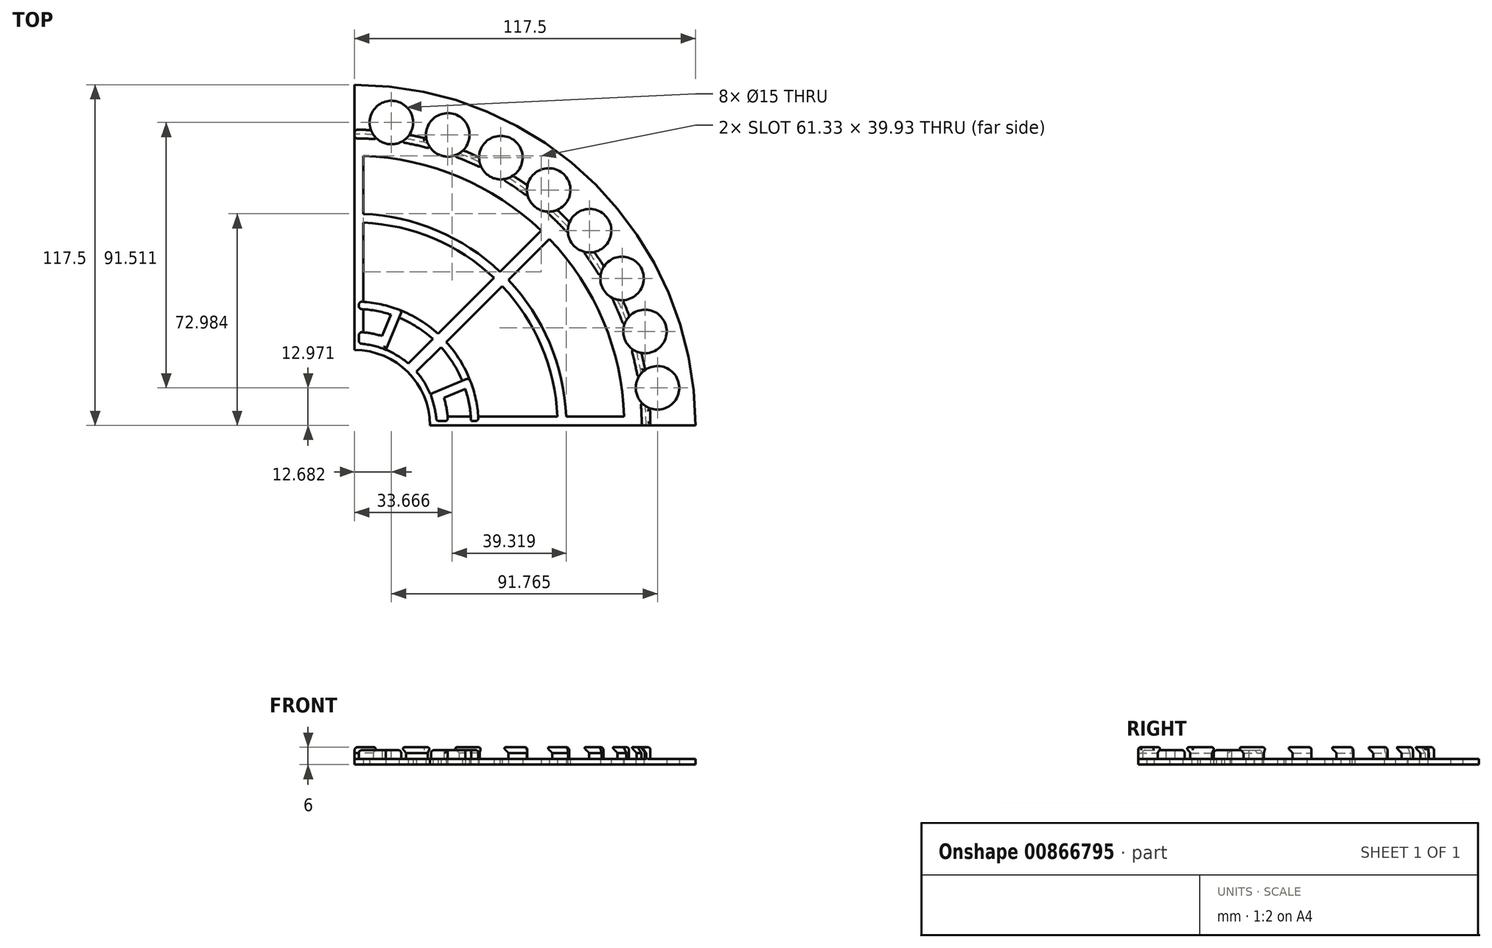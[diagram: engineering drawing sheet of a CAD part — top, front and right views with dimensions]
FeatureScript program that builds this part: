
annotation { "Feature Type Name" : "Feature", "Feature Type Description" : "" }
export const myFeature = defineFeature(function(context is Context, id is Id, definition is map)
    precondition{}
    {
        {
            var Q0;
            Q0=qCreatedBy(makeId("Top.planeOp"),FACE);
            var sketch = newSketch(context, id + "F0", { "sketchPlane" : qUnion([Q0])});
            skCircle(sketch, "E0", {"center": v(0, 0) * mm, "radius": 26 * mm});
            skArc(sketch, "E1", {"start": v(18.5, 21.35) * mm, "mid": v(11.26, 25.9) * mm, "end": v(3, 28.1) * mm});
            skCircle(sketch, "E2", {"center": v(0, 0) * mm, "radius": 42.75 * mm});
            skCircle(sketch, "E3", {"center": v(0, 0) * mm, "radius": 47 * mm});
            skCircle(sketch, "E4", {"center": v(0, 0) * mm, "radius": 93 * mm});
            skCircle(sketch, "E5", {"center": v(0, 0) * mm, "radius": 117.5 * mm});
            skCircle(sketch, "E6", {"center": v(0, 0) * mm, "radius": 36.75 * mm, "construction": true});
            skLineSegment(sketch, "E7", {"start": v(0, 130) * mm, "end": v(0, -133.04) * mm, "construction": true});
            skCircle(sketch, "E8", {"center": v(0, 36.75) * mm, "radius": 3.45 * mm});
            skCircle(sketch, "E9.1.0", {"center": v(-25.99, 25.99) * mm, "radius": 3.45 * mm});
            skCircle(sketch, "E9.2.0", {"center": v(-36.75, 0) * mm, "radius": 3.45 * mm});
            skCircle(sketch, "E9.3.0", {"center": v(-25.99, -25.99) * mm, "radius": 3.45 * mm});
            skCircle(sketch, "E9.4.0", {"center": v(0, -36.75) * mm, "radius": 3.45 * mm});
            skCircle(sketch, "E9.5.0", {"center": v(25.99, -25.99) * mm, "radius": 3.45 * mm});
            skCircle(sketch, "E9.6.0", {"center": v(36.75, 0) * mm, "radius": 3.45 * mm});
            skCircle(sketch, "E9.7.0", {"center": v(25.99, 25.99) * mm, "radius": 3.45 * mm});
            skLineSegment(sketch, "E10", {"start": v(3, 92.95) * mm, "end": v(3, 28.1) * mm});
            skLineSegment(sketch, "E11", {"start": v(28.1, 3) * mm, "end": v(92.95, 3) * mm});
            skCircle(sketch, "E12", {"center": v(0, 0) * mm, "radius": 70 * mm});
            skCircle(sketch, "E13", {"center": v(0, 0) * mm, "radius": 73 * mm});
            skLineSegment(sketch, "E14", {"start": v(0, 0) * mm, "end": v(83.09, 83.09) * mm, "construction": true});
            skLineSegment(sketch, "E15.trimOffspring", {"start": v(18.5, 21.35) * mm, "end": v(64.33, 67.16) * mm});
            skLineSegment(sketch, "E16.trimOffspring", {"start": v(21.35, 18.5) * mm, "end": v(67.16, 64.33) * mm});
            skCircle(sketch, "E17", {"center": v(0, 0) * mm, "radius": 40.2 * mm});
            skLineSegment(sketch, "E18", {"start": v(0, 0) * mm, "end": v(52.17, 125.95) * mm, "construction": true});
            skLineSegment(sketch, "E19.MirrorCS", {"start": v(0, 0) * mm, "end": v(125.95, 52.17) * mm, "construction": true});
            skLineSegment(sketch, "E20", {"start": v(0, 26) * mm, "end": v(0, 117.5) * mm});
            skLineSegment(sketch, "E21", {"start": v(26, 0) * mm, "end": v(93, 0) * mm});
            skCircle(sketch, "E22", {"center": v(0, 0) * mm, "radius": 32.25 * mm});
            skPoint(sketch, "E23", {"position": v(117.5, 0) * mm});
            skPoint(sketch, "E24", {"position": v(0, 93) * mm});
            skLineSegment(sketch, "E25", {"start": v(93, 0) * mm, "end": v(110.05, 0) * mm});
            skLineSegment(sketch, "E26", {"start": v(110.05, 0) * mm, "end": v(117.5, 0) * mm});
            skLineSegment(sketch, "E27.trimOffspring", {"start": v(81.66, 84.48) * mm, "end": v(81.85, 84.67) * mm});
            skLineSegment(sketch, "E28.trimOffspring", {"start": v(84.48, 81.66) * mm, "end": v(84.67, 81.85) * mm});
            skArc(sketch, "E29.trimOffspring", {"start": v(28.1, 3) * mm, "mid": v(25.9, 11.26) * mm, "end": v(21.35, 18.5) * mm});
            skArc(sketch, "E30.trimOffspring", {"start": v(0, 28.25) * mm, "mid": v(-19.98, -19.98) * mm, "end": v(28.25, 0) * mm});
            skSolve(sketch);
        }
        {
            var Q0;
            {var subQ10=sQuery(id+"F0.wireOp",EDGE,"E25");Q0=makeQuery(id+"F0.imprint","IMPRINT",FACE,{"disambiguationData":[TD([[makeQuery(id+"F0.imprint","IMPRINT",EDGE,{"derivedFrom":subQ10}),1.0]])]});}
            var Q1;
            {var subQ0=sQuery(id+"F0.wireOp",EDGE,"E10");var subQ1=sQuery(id+"F0.wireOp",EDGE,"E4");var subQ2=makeQuery(id+"F0.imprint","INTERSECT",VERTEX,{"derivedFrom":[subQ1,subQ0]});Q1=makeQuery(id+"F0.imprint","IMPRINT",FACE,{"disambiguationData":[TD([[makeQuery(id+"F0.imprint","IMPRINT",EDGE,{"disambiguationData":[TD([[subQ2,-1.0]])],"derivedFrom":subQ1}),1.0]])]});}
            var Q2;
            {var subQ0=sQuery(id+"F0.wireOp",EDGE,"E13");var subQ1=sQuery(id+"F0.wireOp",EDGE,"E10");var subQ2=makeQuery(id+"F0.imprint","INTERSECT",VERTEX,{"derivedFrom":[subQ1,subQ0]});Q2=makeQuery(id+"F0.imprint","IMPRINT",FACE,{"disambiguationData":[TD([[makeQuery(id+"F0.imprint","IMPRINT",EDGE,{"disambiguationData":[TD([[subQ2,-1.0]])],"derivedFrom":subQ1}),-1.0]])]});}
            var Q3;
            {var subQ0=sQuery(id+"F0.wireOp",EDGE,"E10");var subQ1=sQuery(id+"F0.wireOp",EDGE,"E3");var subQ2=makeQuery(id+"F0.imprint","INTERSECT",VERTEX,{"derivedFrom":[subQ1,subQ0]});Q3=makeQuery(id+"F0.imprint","IMPRINT",FACE,{"disambiguationData":[TD([[makeQuery(id+"F0.imprint","IMPRINT",EDGE,{"disambiguationData":[TD([[subQ2,-1.0]])],"derivedFrom":subQ1}),-1.0]])]});}
            var Q4;
            {var subQ0=sQuery(id+"F0.wireOp",EDGE,"E10");var subQ1=sQuery(id+"F0.wireOp",EDGE,"E2");var subQ2=makeQuery(id+"F0.imprint","INTERSECT",VERTEX,{"derivedFrom":[subQ1,subQ0]});Q4=makeQuery(id+"F0.imprint","IMPRINT",FACE,{"disambiguationData":[TD([[makeQuery(id+"F0.imprint","IMPRINT",EDGE,{"disambiguationData":[TD([[subQ2,-1.0]])],"derivedFrom":subQ1}),-1.0]])]});}
            var Q5;
            {var subQ0=sQuery(id+"F0.wireOp",EDGE,"E10");var subQ1=sQuery(id+"F0.wireOp",EDGE,"E2");var subQ2=makeQuery(id+"F0.imprint","INTERSECT",VERTEX,{"derivedFrom":[subQ1,subQ0]});Q5=makeQuery(id+"F0.imprint","IMPRINT",FACE,{"disambiguationData":[TD([[makeQuery(id+"F0.imprint","IMPRINT",EDGE,{"disambiguationData":[TD([[subQ2,-1.0]])],"derivedFrom":subQ1}),1.0]])]});}
            var Q6;
            {var subQ1=sQuery(id+"F0.wireOp",EDGE,"E8");var subQ3=sQuery(id+"F0.wireOp",EDGE,"E20");var subQ5=makeQuery(id+"F0.imprint","INTERSECT",VERTEX,{"derivedFrom":[subQ1,subQ3]});Q6=makeQuery(id+"F0.imprint","IMPRINT",FACE,{"disambiguationData":[TD([[makeQuery(id+"F0.imprint","IMPRINT",EDGE,{"disambiguationData":[TD([[subQ5,-1.0]])],"derivedFrom":subQ1}),1.0]])]});}
            var Q7;
            {var subQ0=sQuery(id+"F0.wireOp",EDGE,"E10");var subQ1=sQuery(id+"F0.wireOp",EDGE,"E8");var subQ2=makeQuery(id+"F0.imprint","INTERSECT",VERTEX,{"disambiguationData":[OD(0.0)],"derivedFrom":[subQ1,subQ0]});Q7=makeQuery(id+"F0.imprint","IMPRINT",FACE,{"disambiguationData":[TD([[makeQuery(id+"F0.imprint","IMPRINT",EDGE,{"disambiguationData":[TD([[subQ2,1.0]])],"derivedFrom":subQ0}),-1.0]])]});}
            var Q8;
            {var subQ0=sQuery(id+"F0.wireOp",EDGE,"E20");var subQ1=sQuery(id+"F0.wireOp",EDGE,"E8");var subQ2=makeQuery(id+"F0.imprint","INTERSECT",VERTEX,{"derivedFrom":[subQ1,subQ0]});Q8=makeQuery(id+"F0.imprint","IMPRINT",FACE,{"disambiguationData":[TD([[makeQuery(id+"F0.imprint","IMPRINT",EDGE,{"disambiguationData":[TD([[subQ2,-1.0]])],"derivedFrom":subQ1}),-1.0]])]});}
            var Q9;
            {var subQ16=sQuery(id+"F0.wireOp",EDGE,"E1");Q9=makeQuery(id+"F0.imprint","IMPRINT",FACE,{"disambiguationData":[TD([[makeQuery(id+"F0.imprint","IMPRINT",EDGE,{"derivedFrom":subQ16}),1.0]])]});}
            var Q10;
            {var subQ0=sQuery(id+"F0.wireOp",EDGE,"E15.trimOffspring");var subQ1=sQuery(id+"F0.wireOp",EDGE,"E9.7.0");var subQ2=makeQuery(id+"F0.imprint","INTERSECT",VERTEX,{"disambiguationData":[OD(1.0)],"derivedFrom":[subQ1,subQ0]});Q10=makeQuery(id+"F0.imprint","IMPRINT",FACE,{"disambiguationData":[TD([[makeQuery(id+"F0.imprint","IMPRINT",EDGE,{"disambiguationData":[TD([[subQ2,-1.0]])],"derivedFrom":subQ1}),-1.0]])]});}
            var Q11;
            {var subQ1=sQuery(id+"F0.wireOp",EDGE,"E9.7.0");var subQ6=makeQuery(id+"F0.imprint","INTERSECT",VERTEX,{"derivedFrom":[subQ1,sQuery(id+"F0.wireOp",EDGE,"E17")]});Q11=makeQuery(id+"F0.imprint","IMPRINT",FACE,{"disambiguationData":[TD([[makeQuery(id+"F0.imprint","IMPRINT",EDGE,{"disambiguationData":[TD([[subQ6,1.0]])],"derivedFrom":subQ1}),1.0]])]});}
            var Q12;
            {var subQ2=sQuery(id+"F0.wireOp",EDGE,"E16.trimOffspring");var subQ4=sQuery(id+"F0.wireOp",EDGE,"E2");var subQ5=makeQuery(id+"F0.imprint","INTERSECT",VERTEX,{"derivedFrom":[subQ4,subQ2]});Q12=makeQuery(id+"F0.imprint","IMPRINT",FACE,{"disambiguationData":[TD([[makeQuery(id+"F0.imprint","IMPRINT",EDGE,{"disambiguationData":[TD([[subQ5,-1.0]])],"derivedFrom":subQ4}),1.0]])]});}
            var Q13;
            {var subQ0=sQuery(id+"F0.wireOp",EDGE,"E17");var subQ1=sQuery(id+"F0.wireOp",EDGE,"E9.7.0");var subQ2=makeQuery(id+"F0.imprint","INTERSECT",VERTEX,{"derivedFrom":[subQ1,subQ0]});Q13=makeQuery(id+"F0.imprint","IMPRINT",FACE,{"disambiguationData":[TD([[makeQuery(id+"F0.imprint","IMPRINT",EDGE,{"disambiguationData":[TD([[subQ2,-1.0]])],"derivedFrom":subQ1}),-1.0]])]});}
            var Q14;
            {var subQ0=sQuery(id+"F0.wireOp",EDGE,"E17");var subQ1=sQuery(id+"F0.wireOp",EDGE,"E9.7.0");var subQ2=makeQuery(id+"F0.imprint","INTERSECT",VERTEX,{"derivedFrom":[subQ1,subQ0]});Q14=makeQuery(id+"F0.imprint","IMPRINT",FACE,{"disambiguationData":[TD([[makeQuery(id+"F0.imprint","IMPRINT",EDGE,{"disambiguationData":[TD([[subQ2,1.0]])],"derivedFrom":subQ1}),-1.0]])]});}
            var Q15;
            {var subQ0=sQuery(id+"F0.wireOp",EDGE,"E16.trimOffspring");var subQ1=sQuery(id+"F0.wireOp",EDGE,"E2");var subQ2=makeQuery(id+"F0.imprint","INTERSECT",VERTEX,{"derivedFrom":[subQ1,subQ0]});Q15=makeQuery(id+"F0.imprint","IMPRINT",FACE,{"disambiguationData":[TD([[makeQuery(id+"F0.imprint","IMPRINT",EDGE,{"disambiguationData":[TD([[subQ2,-1.0]])],"derivedFrom":subQ1}),-1.0]])]});}
            var Q16;
            {var subQ0=sQuery(id+"F0.wireOp",EDGE,"E16.trimOffspring");var subQ1=sQuery(id+"F0.wireOp",EDGE,"E3");var subQ2=makeQuery(id+"F0.imprint","INTERSECT",VERTEX,{"derivedFrom":[subQ1,subQ0]});Q16=makeQuery(id+"F0.imprint","IMPRINT",FACE,{"disambiguationData":[TD([[makeQuery(id+"F0.imprint","IMPRINT",EDGE,{"disambiguationData":[TD([[subQ2,-1.0]])],"derivedFrom":subQ1}),-1.0]])]});}
            var Q17;
            {var subQ0=sQuery(id+"F0.wireOp",EDGE,"E16.trimOffspring");var subQ1=sQuery(id+"F0.wireOp",EDGE,"E12");var subQ2=makeQuery(id+"F0.imprint","INTERSECT",VERTEX,{"derivedFrom":[subQ1,subQ0]});Q17=makeQuery(id+"F0.imprint","IMPRINT",FACE,{"disambiguationData":[TD([[makeQuery(id+"F0.imprint","IMPRINT",EDGE,{"disambiguationData":[TD([[subQ2,-1.0]])],"derivedFrom":subQ1}),-1.0]])]});}
            var Q18;
            {var subQ0=sQuery(id+"F0.wireOp",EDGE,"E13");var subQ1=sQuery(id+"F0.wireOp",EDGE,"E10");var subQ2=makeQuery(id+"F0.imprint","INTERSECT",VERTEX,{"derivedFrom":[subQ1,subQ0]});Q18=makeQuery(id+"F0.imprint","IMPRINT",FACE,{"disambiguationData":[TD([[makeQuery(id+"F0.imprint","IMPRINT",EDGE,{"disambiguationData":[TD([[subQ2,-1.0]])],"derivedFrom":subQ1}),1.0]])]});}
            var Q19;
            {var subQ0=sQuery(id+"F0.wireOp",EDGE,"E15.trimOffspring");var subQ1=sQuery(id+"F0.wireOp",EDGE,"E4");var subQ2=makeQuery(id+"F0.imprint","INTERSECT",VERTEX,{"derivedFrom":[subQ1,subQ0]});Q19=makeQuery(id+"F0.imprint","IMPRINT",FACE,{"disambiguationData":[TD([[makeQuery(id+"F0.imprint","IMPRINT",EDGE,{"disambiguationData":[TD([[subQ2,1.0]])],"derivedFrom":subQ1}),1.0]])]});}
            var Q20;
            {var subQ0=sQuery(id+"F0.wireOp",EDGE,"E12");var subQ1=sQuery(id+"F0.wireOp",EDGE,"E11");var subQ2=makeQuery(id+"F0.imprint","INTERSECT",VERTEX,{"derivedFrom":[subQ1,subQ0]});Q20=makeQuery(id+"F0.imprint","IMPRINT",FACE,{"disambiguationData":[TD([[makeQuery(id+"F0.imprint","IMPRINT",EDGE,{"disambiguationData":[TD([[subQ2,-1.0]])],"derivedFrom":subQ1}),1.0]])]});}
            var Q21;
            {var subQ0=sQuery(id+"F0.wireOp",EDGE,"E11");var subQ1=sQuery(id+"F0.wireOp",EDGE,"E9.6.0");var subQ2=makeQuery(id+"F0.imprint","INTERSECT",VERTEX,{"disambiguationData":[OD(1.0)],"derivedFrom":[subQ1,subQ0]});Q21=makeQuery(id+"F0.imprint","IMPRINT",FACE,{"disambiguationData":[TD([[makeQuery(id+"F0.imprint","IMPRINT",EDGE,{"disambiguationData":[TD([[subQ2,-1.0]])],"derivedFrom":subQ1}),-1.0]])]});}
            var Q22;
            {var subQ0=sQuery(id+"F0.wireOp",EDGE,"E11");var subQ1=sQuery(id+"F0.wireOp",EDGE,"E9.6.0");var subQ5=makeQuery(id+"F0.imprint","INTERSECT",VERTEX,{"disambiguationData":[OD(1.0)],"derivedFrom":[subQ1,subQ0]});Q22=makeQuery(id+"F0.imprint","IMPRINT",FACE,{"disambiguationData":[TD([[makeQuery(id+"F0.imprint","IMPRINT",EDGE,{"disambiguationData":[TD([[subQ5,-1.0]])],"derivedFrom":subQ1}),1.0]])]});}
            var Q23;
            {var subQ0=sQuery(id+"F0.wireOp",EDGE,"E11");var subQ1=sQuery(id+"F0.wireOp",EDGE,"E9.6.0");var subQ2=makeQuery(id+"F0.imprint","INTERSECT",VERTEX,{"disambiguationData":[OD(0.0)],"derivedFrom":[subQ1,subQ0]});Q23=makeQuery(id+"F0.imprint","IMPRINT",FACE,{"disambiguationData":[TD([[makeQuery(id+"F0.imprint","IMPRINT",EDGE,{"disambiguationData":[TD([[subQ2,-1.0]])],"derivedFrom":subQ0}),-1.0]])]});}
            var Q24;
            {var subQ0=sQuery(id+"F0.wireOp",EDGE,"E11");var subQ1=sQuery(id+"F0.wireOp",EDGE,"E2");var subQ2=makeQuery(id+"F0.imprint","INTERSECT",VERTEX,{"derivedFrom":[subQ1,subQ0]});Q24=makeQuery(id+"F0.imprint","IMPRINT",FACE,{"disambiguationData":[TD([[makeQuery(id+"F0.imprint","IMPRINT",EDGE,{"disambiguationData":[TD([[subQ2,1.0]])],"derivedFrom":subQ1}),1.0]])]});}
            var Q25;
            {var subQ0=sQuery(id+"F0.wireOp",EDGE,"E11");var subQ1=sQuery(id+"F0.wireOp",EDGE,"E2");var subQ2=makeQuery(id+"F0.imprint","INTERSECT",VERTEX,{"derivedFrom":[subQ1,subQ0]});Q25=makeQuery(id+"F0.imprint","IMPRINT",FACE,{"disambiguationData":[TD([[makeQuery(id+"F0.imprint","IMPRINT",EDGE,{"disambiguationData":[TD([[subQ2,1.0]])],"derivedFrom":subQ1}),-1.0]])]});}
            var Q26;
            {var subQ0=sQuery(id+"F0.wireOp",EDGE,"E11");var subQ1=sQuery(id+"F0.wireOp",EDGE,"E3");var subQ2=makeQuery(id+"F0.imprint","INTERSECT",VERTEX,{"derivedFrom":[subQ1,subQ0]});Q26=makeQuery(id+"F0.imprint","IMPRINT",FACE,{"disambiguationData":[TD([[makeQuery(id+"F0.imprint","IMPRINT",EDGE,{"disambiguationData":[TD([[subQ2,1.0]])],"derivedFrom":subQ1}),-1.0]])]});}
            var Q27;
            {var subQ0=sQuery(id+"F0.wireOp",EDGE,"E12");var subQ1=sQuery(id+"F0.wireOp",EDGE,"E11");var subQ2=makeQuery(id+"F0.imprint","INTERSECT",VERTEX,{"derivedFrom":[subQ1,subQ0]});Q27=makeQuery(id+"F0.imprint","IMPRINT",FACE,{"disambiguationData":[TD([[makeQuery(id+"F0.imprint","IMPRINT",EDGE,{"disambiguationData":[TD([[subQ2,-1.0]])],"derivedFrom":subQ1}),-1.0]])]});}
            var Q28;
            {var subQ0=sQuery(id+"F0.wireOp",EDGE,"E11");var subQ1=sQuery(id+"F0.wireOp",EDGE,"E4");var subQ2=makeQuery(id+"F0.imprint","INTERSECT",VERTEX,{"derivedFrom":[subQ1,subQ0]});Q28=makeQuery(id+"F0.imprint","IMPRINT",FACE,{"disambiguationData":[TD([[makeQuery(id+"F0.imprint","IMPRINT",EDGE,{"disambiguationData":[TD([[subQ2,1.0]])],"derivedFrom":subQ0}),-1.0]])]});}
            var Q29;
            {var subQ0=sQuery(id+"F0.wireOp",EDGE,"E15.trimOffspring");var subQ1=sQuery(id+"F0.wireOp",EDGE,"E2");var subQ2=makeQuery(id+"F0.imprint","INTERSECT",VERTEX,{"derivedFrom":[subQ1,subQ0]});Q29=makeQuery(id+"F0.imprint","IMPRINT",FACE,{"disambiguationData":[TD([[makeQuery(id+"F0.imprint","IMPRINT",EDGE,{"disambiguationData":[TD([[subQ2,-1.0]])],"derivedFrom":subQ1}),1.0]])]});}
            var Q30;
            {var subQ0=sQuery(id+"F0.wireOp",EDGE,"E11");var subQ1=sQuery(id+"F0.wireOp",EDGE,"E2");var subQ2=makeQuery(id+"F0.imprint","INTERSECT",VERTEX,{"derivedFrom":[subQ1,subQ0]});Q30=makeQuery(id+"F0.imprint","IMPRINT",FACE,{"disambiguationData":[TD([[makeQuery(id+"F0.imprint","IMPRINT",EDGE,{"disambiguationData":[TD([[subQ2,-1.0]])],"derivedFrom":subQ1}),1.0]])]});}
            extrude(context, id + "F1", {"entities" : qUnion([Q0, Q1, Q2, Q3, Q4, Q5, Q6, Q7, Q8, Q9, Q10, Q11, Q12, Q13, Q14, Q15, Q16, Q17, Q18, Q19, Q20, Q21, Q22, Q23, Q24, Q25, Q26, Q27, Q28, Q29, Q30]), "depth" : 2 * mm, "offsetDistance" : 25 * mm});
        }
        {
            var Q0;
            Q0=qCreatedBy(makeId("Top.planeOp"),FACE);
            var sketch = newSketch(context, id + "F2", { "sketchPlane" : qUnion([Q0])});
            skLineSegment(sketch, "E31.2", {"start": v(26.1, 10.81) * mm, "end": v(39.5, 16.36) * mm});
            skLineSegment(sketch, "E31.3", {"start": v(10.81, 26.1) * mm, "end": v(16.36, 39.5) * mm});
            skArc(sketch, "E32.1", {"start": v(10.81, 26.1) * mm, "mid": v(6.25, 27.55) * mm, "end": v(1.5, 28.21) * mm});
            skArc(sketch, "E32.2", {"start": v(28.21, 1.5) * mm, "mid": v(27.55, 6.25) * mm, "end": v(26.1, 10.81) * mm});
            skArc(sketch, "E32.3", {"start": v(16.36, 39.5) * mm, "mid": v(9.07, 41.78) * mm, "end": v(1.5, 42.72) * mm});
            skArc(sketch, "E32.4", {"start": v(12.57, 38.18) * mm, "mid": v(7.1, 39.57) * mm, "end": v(1.5, 40.17) * mm});
            skLineSegment(sketch, "E33.0", {"start": v(1.5, 28.21) * mm, "end": v(1.5, 32.22) * mm});
            skLineSegment(sketch, "E34.0", {"start": v(28.21, 1.5) * mm, "end": v(32.22, 1.5) * mm});
            skArc(sketch, "E35.trimOffspring", {"start": v(42.72, 1.5) * mm, "mid": v(41.78, 9.07) * mm, "end": v(39.5, 16.36) * mm});
            skArc(sketch, "E36.trimOffspring", {"start": v(40.17, 1.5) * mm, "mid": v(39.57, 7.1) * mm, "end": v(38.18, 12.57) * mm});
            skLineSegment(sketch, "E37.0", {"start": v(9.52, 30.81) * mm, "end": v(12.57, 38.18) * mm});
            skLineSegment(sketch, "E38.0", {"start": v(30.81, 9.52) * mm, "end": v(38.18, 12.57) * mm});
            skPoint(sketch, "E39.orphan", {"position": v(3, 40.09) * mm});
            skPoint(sketch, "E40.orphan", {"position": v(3, 28.1) * mm});
            skPoint(sketch, "E41.orphan", {"position": v(28.1, 3) * mm});
            skPoint(sketch, "E42.orphan", {"position": v(40.09, 3) * mm});
            skPoint(sketch, "E43.orphan", {"position": v(0, 26) * mm});
            skPoint(sketch, "E44.orphan", {"position": v(26, 0) * mm});
            skCircle(sketch, "E45.0", {"center": v(36.75, 0) * mm, "radius": 3.45 * mm, "construction": true});
            skArc(sketch, "E46.0", {"start": v(32.22, 1.5) * mm, "mid": v(31.77, 5.55) * mm, "end": v(30.81, 9.52) * mm});
            skCircle(sketch, "E47.1", {"center": v(0, 36.75) * mm, "radius": 3.45 * mm, "construction": true});
            skLineSegment(sketch, "E48.trimOffspring", {"start": v(40.17, 1.5) * mm, "end": v(42.72, 1.5) * mm});
            skLineSegment(sketch, "E49.trimOffspring", {"start": v(1.5, 40.17) * mm, "end": v(1.5, 42.72) * mm});
            skArc(sketch, "E50.trimOffspring", {"start": v(9.52, 30.81) * mm, "mid": v(5.55, 31.77) * mm, "end": v(1.5, 32.22) * mm});
            skSolve(sketch);
        }
        {
            var Q0;
            Q0 = qSketchRegion(id + "F2", true);
            extrude(context, id + "F3", {"entities" : qUnion([Q0]), "operationType" : NewBodyOperationType.ADD, "depth" : 5 * mm, "offsetDistance" : 25 * mm});
        }
        {
            var Q0;
            Q0=makeQuery(id+"F1.opExtrude","SWEPT_FACE",FACE,{"disambiguationData":[OSD([sQuery(id+"F0.wireOp",EDGE,"E20")])]});
            var sketch = newSketch(context, id + "F4", { "sketchPlane" : qUnion([Q0])});
            skLineSegment(sketch, "E51", {"start": v(-102, 6) * mm, "end": v(-99, 6) * mm});
            skLineSegment(sketch, "E52.0", {"start": v(-42.75, 2) * mm, "end": v(-117.5, 2) * mm});
            skLineSegment(sketch, "E53", {"start": v(-102, 6) * mm, "end": v(-102, 2) * mm});
            skLineSegment(sketch, "E54", {"start": v(-100.5, 2) * mm, "end": v(-100.5, 4) * mm});
            skLineSegment(sketch, "E55", {"start": v(-100.5, 4) * mm, "end": v(-99, 6) * mm});
            skSolve(sketch);
        }
        {
            var Q0;
            Q0=qCreatedBy(makeId("Front.planeOp"),FACE);
            var sketch = newSketch(context, id + "F5", { "sketchPlane" : qUnion([Q0])});
            skLineSegment(sketch, "E56", {"start": v(0, 34.31) * mm, "end": v(0, -23.12) * mm, "construction": true});
            skSolve(sketch);
        }
        {
            var Q0;
            Q0=makeQuery(id+"F4.imprint","IMPRINT",FACE,{"disambiguationData":[TD([[makeQuery(id+"F4.imprint","IMPRINT",EDGE,{"derivedFrom":sQuery(id+"F4.wireOp",EDGE,"E51")}),-1.0]])]});
            var Q1;
            Q1=sQuery(id+"F5.wireOp",EDGE,"E56");
            revolve(context, id + "F6", {"operationType" : NewBodyOperationType.ADD, "surfaceOperationType" : NewSurfaceOperationType.NEW, "entities" : qUnion([Q0]), "axis" : qUnion([Q1]), "revolveType" : RevolveType.FULL});
        }
        {
            var Q0;
            {var subQ0=sQuery(id+"F0.wireOp",EDGE,"E20");var subQ3=sQuery(id+"F0.wireOp",EDGE,"E26");var subQ4=sQuery(id+"F0.wireOp",EDGE,"E25");var subQ5=sQuery(id+"F0.wireOp",EDGE,"E21");var subQ7=sQuery(id+"F0.wireOp",EDGE,"E5");var subQ8=makeQuery(id+"F1.opExtrude","SWEPT_FACE",FACE,{"disambiguationData":[OSD([subQ7])]});var subQ10=sQuery(id+"F0.wireOp",EDGE,"E17");var subQ11=sQuery(id+"F0.wireOp",EDGE,"E11");var subQ12=sQuery(id+"F0.wireOp",EDGE,"E16.trimOffspring");var subQ14=sQuery(id+"F0.wireOp",EDGE,"E4");var subQ16=sQuery(id+"F0.wireOp",EDGE,"E13");var subQ23=sQuery(id+"F0.wireOp",EDGE,"E29.trimOffspring");var subQ24=sQuery(id+"F0.wireOp",EDGE,"E15.trimOffspring");var subQ29=sQuery(id+"F0.wireOp",EDGE,"E12");var subQ31=sQuery(id+"F0.wireOp",EDGE,"E2");var subQ37=sQuery(id+"F0.wireOp",EDGE,"E1");var subQ38=sQuery(id+"F0.wireOp",EDGE,"E10");var subQ49=sQuery(id+"F0.wireOp",EDGE,"E0");Q0=makeQuery(id+"F6.boolean.opBoolean","SPLIT",FACE,{"disambiguationData":[TD([subQ8])],"derivedFrom":makeQuery(id+"F3.boolean.opBoolean","SPLIT",FACE,{"disambiguationData":[TD([makeQuery(id+"F1.opExtrude","SWEPT_FACE",FACE,{"disambiguationData":[OSD([subQ49])]})])],"derivedFrom":makeQuery(id+"F1.opExtrude","CAP_FACE",FACE,{"disambiguationData":[OSD([subQ49,subQ37,subQ31,subQ14,subQ7,subQ38,subQ11,subQ29,subQ16,subQ24,subQ12,subQ10,subQ0,subQ5,subQ4,subQ3,subQ23])],"isStart":false})})});}
            var sketch = newSketch(context, id + "F7", { "sketchPlane" : qUnion([Q0])});
            skCircle(sketch, "E57.0", {"center": v(0, 0) * mm, "radius": 102 * mm});
            skCircle(sketch, "E57.1", {"center": v(0, 0) * mm, "radius": 99 * mm});
            skLineSegment(sketch, "E57.2", {"start": v(93, 0) * mm, "end": v(110.05, 0) * mm});
            skLineSegment(sketch, "E57.3", {"start": v(0, 42.75) * mm, "end": v(0, 117.5) * mm});
            skSolve(sketch);
        }
        {
            var Q0;
            {var subQ0=sQuery(id+"F7.wireOp",EDGE,"E57.3");var subQ1=sQuery(id+"F7.wireOp",EDGE,"E57.0");var subQ2=makeQuery(id+"F7.imprint","INTERSECT",VERTEX,{"derivedFrom":[subQ1,subQ0]});Q0=makeQuery(id+"F7.imprint","IMPRINT",FACE,{"disambiguationData":[TD([[makeQuery(id+"F7.imprint","IMPRINT",EDGE,{"disambiguationData":[TD([[subQ2,-1.0]])],"derivedFrom":subQ1}),1.0]])]});}
            extrude(context, id + "F8", {"entities" : qUnion([Q0]), "operationType" : NewBodyOperationType.REMOVE, "endBound" : BoundingType.THROUGH_ALL, "depth" : 25 * mm, "offsetDistance" : 25 * mm});
        }
        {
            var Q0;
            Q0=makeQuery(id+"F3.boolean.opBoolean","MERGE",FACE,{"derivedFrom":[makeQuery(id+"F1.opExtrude","CAP_FACE",FACE,{"disambiguationData":[OSD([sQuery(id+"F0.wireOp",EDGE,"E0"),sQuery(id+"F0.wireOp",EDGE,"E1"),sQuery(id+"F0.wireOp",EDGE,"E2"),sQuery(id+"F0.wireOp",EDGE,"E4"),sQuery(id+"F0.wireOp",EDGE,"E5"),sQuery(id+"F0.wireOp",EDGE,"E10"),sQuery(id+"F0.wireOp",EDGE,"E11"),sQuery(id+"F0.wireOp",EDGE,"E12"),sQuery(id+"F0.wireOp",EDGE,"E13"),sQuery(id+"F0.wireOp",EDGE,"E15.trimOffspring"),sQuery(id+"F0.wireOp",EDGE,"E16.trimOffspring"),sQuery(id+"F0.wireOp",EDGE,"E17"),sQuery(id+"F0.wireOp",EDGE,"E20"),sQuery(id+"F0.wireOp",EDGE,"E21"),sQuery(id+"F0.wireOp",EDGE,"E25"),sQuery(id+"F0.wireOp",EDGE,"E26"),sQuery(id+"F0.wireOp",EDGE,"E29.trimOffspring")])],"isStart":true}),makeQuery(id+"F3.opExtrude","CAP_FACE",FACE,{"disambiguationData":[OSD([sQuery(id+"F2.wireOp",EDGE,"E31.0"),sQuery(id+"F2.wireOp",EDGE,"E31.3"),sQuery(id+"F2.wireOp",EDGE,"E32.1"),sQuery(id+"F2.wireOp",EDGE,"E32.3"),sQuery(id+"F2.wireOp",EDGE,"E32.4"),sQuery(id+"F2.wireOp",EDGE,"E33.0"),sQuery(id+"F2.wireOp",EDGE,"8e3e6910-3747-4ed9-b88e-42e2a95604ab.trimOffspring"),sQuery(id+"F2.wireOp",EDGE,"E37.0")])],"isStart":true}),makeQuery(id+"F3.opExtrude","CAP_FACE",FACE,{"disambiguationData":[OSD([sQuery(id+"F2.wireOp",EDGE,"E31.1"),sQuery(id+"F2.wireOp",EDGE,"E31.2"),sQuery(id+"F2.wireOp",EDGE,"E32.0"),sQuery(id+"F2.wireOp",EDGE,"E32.2"),sQuery(id+"F2.wireOp",EDGE,"E34.0"),sQuery(id+"F2.wireOp",EDGE,"E35.trimOffspring"),sQuery(id+"F2.wireOp",EDGE,"E36.trimOffspring"),sQuery(id+"F2.wireOp",EDGE,"E38.0")])],"isStart":true})]});
            var sketch = newSketch(context, id + "F9", { "sketchPlane" : qUnion([Q0])});
            skArc(sketch, "E58.0", {"start": v(117.5, 0) * mm, "mid": v(83.09, -83.09) * mm, "end": v(0, -117.5) * mm});
            skArc(sketch, "E58.1", {"start": v(92.95, -3) * mm, "mid": v(85.73, -36.05) * mm, "end": v(67.16, -64.33) * mm});
            skLineSegment(sketch, "E58.2", {"start": v(26, 0) * mm, "end": v(117.5, 0) * mm});
            skLineSegment(sketch, "E58.3", {"start": v(0, -26) * mm, "end": v(0, -117.5) * mm});
            skLineSegment(sketch, "E59", {"start": v(92.95, -3) * mm, "end": v(117.46, -3) * mm});
            skLineSegment(sketch, "E60", {"start": v(3, -92.95) * mm, "end": v(3, -117.46) * mm});
            skPoint(sketch, "E61", {"position": v(105.2, -3) * mm});
            skArc(sketch, "E62", {"start": v(105.2, -3) * mm, "mid": v(74.42, -74.42) * mm, "end": v(3, -105.2) * mm, "construction": true});
            skCircle(sketch, "E63", {"center": v(105.2, -3) * mm, "radius": 10 * mm, "construction": true});
            skCircle(sketch, "E64", {"center": v(3, -105.2) * mm, "radius": 10 * mm, "construction": true});
            skCircle(sketch, "E65", {"center": v(104.45, -12.97) * mm, "radius": 7.5 * mm});
            skLineSegment(sketch, "E66", {"start": v(0, 0) * mm, "end": v(12.97, -104.45) * mm, "construction": true});
            skCircle(sketch, "E67.1.0", {"center": v(100.13, -32.41) * mm, "radius": 7.5 * mm});
            skCircle(sketch, "E67.2.0", {"center": v(92.24, -50.7) * mm, "radius": 7.5 * mm});
            skCircle(sketch, "E67.3.0", {"center": v(81.04, -67.16) * mm, "radius": 7.5 * mm});
            skCircle(sketch, "E67.4.0", {"center": v(66.94, -81.22) * mm, "radius": 7.5 * mm});
            skCircle(sketch, "E67.5.0", {"center": v(50.44, -92.38) * mm, "radius": 7.5 * mm});
            skCircle(sketch, "E67.6.0", {"center": v(32.14, -100.22) * mm, "radius": 7.5 * mm});
            skCircle(sketch, "E67.7.0", {"center": v(12.68, -104.48) * mm, "radius": 7.5 * mm});
            skLineSegment(sketch, "E67.anchor1", {"start": v(0, 0) * mm, "end": v(104.45, -12.97) * mm, "construction": true});
            skLineSegment(sketch, "E67.anchor2", {"start": v(0, 0) * mm, "end": v(12.68, -104.48) * mm, "construction": true});
            skSolve(sketch);
        }
        {
            var Q0;
            Q0=makeQuery(id+"F9.imprint","IMPRINT",FACE,{"disambiguationData":[TD([[makeQuery(id+"F9.imprint","IMPRINT",EDGE,{"derivedFrom":sQuery(id+"F9.wireOp",EDGE,"E65")}),1.0]])]});
            var Q1;
            Q1=makeQuery(id+"F9.imprint","IMPRINT",FACE,{"disambiguationData":[TD([[makeQuery(id+"F9.imprint","IMPRINT",EDGE,{"derivedFrom":sQuery(id+"F9.wireOp",EDGE,"E67.1.0")}),1.0]])]});
            var Q2;
            Q2=makeQuery(id+"F9.imprint","IMPRINT",FACE,{"disambiguationData":[TD([[makeQuery(id+"F9.imprint","IMPRINT",EDGE,{"derivedFrom":sQuery(id+"F9.wireOp",EDGE,"E67.2.0")}),1.0]])]});
            var Q3;
            Q3=makeQuery(id+"F9.imprint","IMPRINT",FACE,{"disambiguationData":[TD([[makeQuery(id+"F9.imprint","IMPRINT",EDGE,{"derivedFrom":sQuery(id+"F9.wireOp",EDGE,"E67.3.0")}),1.0]])]});
            var Q4;
            Q4=makeQuery(id+"F9.imprint","IMPRINT",FACE,{"disambiguationData":[TD([[makeQuery(id+"F9.imprint","IMPRINT",EDGE,{"derivedFrom":sQuery(id+"F9.wireOp",EDGE,"E67.4.0")}),1.0]])]});
            var Q5;
            Q5=makeQuery(id+"F9.imprint","IMPRINT",FACE,{"disambiguationData":[TD([[makeQuery(id+"F9.imprint","IMPRINT",EDGE,{"derivedFrom":sQuery(id+"F9.wireOp",EDGE,"E67.5.0")}),1.0]])]});
            var Q6;
            Q6=makeQuery(id+"F9.imprint","IMPRINT",FACE,{"disambiguationData":[TD([[makeQuery(id+"F9.imprint","IMPRINT",EDGE,{"derivedFrom":sQuery(id+"F9.wireOp",EDGE,"E67.6.0")}),1.0]])]});
            var Q7;
            Q7=makeQuery(id+"F9.imprint","IMPRINT",FACE,{"disambiguationData":[TD([[makeQuery(id+"F9.imprint","IMPRINT",EDGE,{"derivedFrom":sQuery(id+"F9.wireOp",EDGE,"E67.7.0")}),1.0]])]});
            extrude(context, id + "F10", {"entities" : qUnion([Q0, Q1, Q2, Q3, Q4, Q5, Q6, Q7]), "operationType" : NewBodyOperationType.REMOVE, "endBound" : BoundingType.THROUGH_ALL, "oppositeDirection" : true, "depth" : 25 * mm, "offsetDistance" : 25 * mm});
        }
        {
            var Q0;
            Q0=makeQuery(id+"F3.opExtrude","CAP_EDGE",EDGE,{"disambiguationData":[OSD([sQuery(id+"F2.wireOp",EDGE,"E33.0")])],"isStart":false});
            var Q1;
            Q1=makeQuery(id+"F3.opExtrude","CAP_EDGE",EDGE,{"disambiguationData":[OSD([sQuery(id+"F2.wireOp",EDGE,"E31.3")])],"isStart":false});
            var Q2;
            Q2=makeQuery(id+"F3.opExtrude","CAP_EDGE",EDGE,{"disambiguationData":[OSD([sQuery(id+"F2.wireOp",EDGE,"E32.3")])],"isStart":false});
            var Q3;
            Q3=makeQuery(id+"F3.opExtrude","CAP_EDGE",EDGE,{"disambiguationData":[OSD([sQuery(id+"F2.wireOp",EDGE,"8e3e6910-3747-4ed9-b88e-42e2a95604ab.trimOffspring")])],"isStart":false});
            var Q4;
            Q4=makeQuery(id+"F3.opExtrude","CAP_EDGE",EDGE,{"disambiguationData":[OSD([sQuery(id+"F2.wireOp",EDGE,"E32.0")])],"isStart":false});
            var Q5;
            Q5=makeQuery(id+"F3.opExtrude","CAP_EDGE",EDGE,{"disambiguationData":[OSD([sQuery(id+"F2.wireOp",EDGE,"E31.2")])],"isStart":false});
            var Q6;
            Q6=makeQuery(id+"F3.opExtrude","CAP_EDGE",EDGE,{"disambiguationData":[OSD([sQuery(id+"F2.wireOp",EDGE,"E34.0")])],"isStart":false});
            var Q7;
            Q7=makeQuery(id+"F3.opExtrude","CAP_EDGE",EDGE,{"disambiguationData":[OSD([sQuery(id+"F2.wireOp",EDGE,"E35.trimOffspring")])],"isStart":false});
            var Q8;
            Q8=makeQuery(id+"F8.boolean.opBoolean","INTERSECT",EDGE,{"derivedFrom":[makeQuery(id+"F6.opRevolve","SWEPT_FACE",FACE,{"disambiguationData":[OSD([sQuery(id+"F4.wireOp",EDGE,"E51")])]}),makeQuery(id+"F8.opExtrude","SWEPT_FACE",FACE,{"disambiguationData":[OSD([sQuery(id+"F7.wireOp",EDGE,"E57.2")])]})]});
            var Q9;
            Q9=makeQuery(id+"F8.boolean.opBoolean","INTERSECT",EDGE,{"derivedFrom":[makeQuery(id+"F6.opRevolve","SWEPT_FACE",FACE,{"disambiguationData":[OSD([sQuery(id+"F4.wireOp",EDGE,"E51")])]}),makeQuery(id+"F8.opExtrude","SWEPT_FACE",FACE,{"disambiguationData":[OSD([sQuery(id+"F7.wireOp",EDGE,"E57.3")])]})]});
            var Q10;
            Q10=makeQuery(id+"F3.opExtrude","CAP_EDGE",EDGE,{"disambiguationData":[OSD([sQuery(id+"F2.wireOp",EDGE,"E49.trimOffspring")])],"isStart":false});
            var Q11;
            Q11=makeQuery(id+"F3.opExtrude","CAP_EDGE",EDGE,{"disambiguationData":[OSD([sQuery(id+"F2.wireOp",EDGE,"E32.1")])],"isStart":false});
            var Q12;
            Q12=makeQuery(id+"F3.opExtrude","SWEPT_EDGE",EDGE,{"disambiguationData":[OSD([sQuery(id+"F2.wireOp",EDGE,"E33.0"),sQuery(id+"F2.wireOp",EDGE,"E50.trimOffspring")])]});
            var Q13;
            Q13=makeQuery(id+"F3.opExtrude","SWEPT_EDGE",EDGE,{"disambiguationData":[OSD([sQuery(id+"F2.wireOp",EDGE,"E32.4"),sQuery(id+"F2.wireOp",EDGE,"E49.trimOffspring")])]});
            var Q14;
            Q14=makeQuery(id+"F3.opExtrude","SWEPT_EDGE",EDGE,{"disambiguationData":[OSD([sQuery(id+"F2.wireOp",EDGE,"E32.3"),sQuery(id+"F2.wireOp",EDGE,"E49.trimOffspring")])]});
            var Q15;
            Q15=makeQuery(id+"F3.opExtrude","SWEPT_EDGE",EDGE,{"disambiguationData":[OSD([sQuery(id+"F2.wireOp",EDGE,"E32.1"),sQuery(id+"F2.wireOp",EDGE,"E33.0")])]});
            var Q16;
            Q16=makeQuery(id+"F3.opExtrude","SWEPT_EDGE",EDGE,{"disambiguationData":[OSD([sQuery(id+"F2.wireOp",EDGE,"E34.0"),sQuery(id+"F2.wireOp",EDGE,"E46.0")])]});
            var Q17;
            Q17=makeQuery(id+"F3.opExtrude","SWEPT_EDGE",EDGE,{"disambiguationData":[OSD([sQuery(id+"F2.wireOp",EDGE,"E35.trimOffspring"),sQuery(id+"F2.wireOp",EDGE,"E48.trimOffspring")])]});
            var Q18;
            Q18=makeQuery(id+"F3.opExtrude","SWEPT_EDGE",EDGE,{"disambiguationData":[OSD([sQuery(id+"F2.wireOp",EDGE,"E32.2"),sQuery(id+"F2.wireOp",EDGE,"E34.0")])]});
            var Q19;
            {var subQ0=sQuery(id+"F2.wireOp",EDGE,"E31.2");var subQ1=sQuery(id+"F2.wireOp",EDGE,"E32.2");Q19=makeQuery(id+"F3.boolean.opBoolean","SPLIT",EDGE,{"disambiguationData":[topologyDisambiguationEdgeConnected([makeQuery(id+"F3.opExtrude","SWEPT_FACE",FACE,{"disambiguationData":[OSD([subQ1])]})])],"derivedFrom":makeQuery(id+"F3.opExtrude","SWEPT_EDGE",EDGE,{"disambiguationData":[OSD([subQ0,subQ1])]})});}
            var Q20;
            Q20=makeQuery(id+"F3.opExtrude","SWEPT_EDGE",EDGE,{"disambiguationData":[OSD([sQuery(id+"F2.wireOp",EDGE,"E31.2"),sQuery(id+"F2.wireOp",EDGE,"E35.trimOffspring")])]});
            var Q21;
            Q21=makeQuery(id+"F3.opExtrude","CAP_EDGE",EDGE,{"disambiguationData":[OSD([sQuery(id+"F2.wireOp",EDGE,"E32.2")])],"isStart":false});
            var Q22;
            Q22=makeQuery(id+"F3.opExtrude","CAP_EDGE",EDGE,{"disambiguationData":[OSD([sQuery(id+"F2.wireOp",EDGE,"E48.trimOffspring")])],"isStart":false});
            var Q23;
            Q23=makeQuery(id+"F3.opExtrude","SWEPT_EDGE",EDGE,{"disambiguationData":[OSD([sQuery(id+"F2.wireOp",EDGE,"E31.3"),sQuery(id+"F2.wireOp",EDGE,"E32.3")])]});
            var Q24;
            Q24=makeQuery(id+"F10.boolean.opBoolean","INTERSECT",EDGE,{"disambiguationData":[OD(0.0)],"derivedFrom":[makeQuery(id+"F6.opRevolve","SWEPT_FACE",FACE,{"disambiguationData":[OSD([sQuery(id+"F4.wireOp",EDGE,"E51")])]}),makeQuery(id+"F10.opExtrude","SWEPT_FACE",FACE,{"disambiguationData":[OSD([sQuery(id+"F9.wireOp",EDGE,"E67.7.0")])]})]});
            var Q25;
            Q25=makeQuery(id+"F10.boolean.opBoolean","INTERSECT",EDGE,{"disambiguationData":[OD(1.0)],"derivedFrom":[makeQuery(id+"F6.opRevolve","SWEPT_FACE",FACE,{"disambiguationData":[OSD([sQuery(id+"F4.wireOp",EDGE,"E51")])]}),makeQuery(id+"F10.opExtrude","SWEPT_FACE",FACE,{"disambiguationData":[OSD([sQuery(id+"F9.wireOp",EDGE,"E67.6.0")])]})]});
            var Q26;
            Q26=makeQuery(id+"F10.boolean.opBoolean","INTERSECT",EDGE,{"disambiguationData":[OD(1.0)],"derivedFrom":[makeQuery(id+"F6.opRevolve","SWEPT_FACE",FACE,{"disambiguationData":[OSD([sQuery(id+"F4.wireOp",EDGE,"E51")])]}),makeQuery(id+"F10.opExtrude","SWEPT_FACE",FACE,{"disambiguationData":[OSD([sQuery(id+"F9.wireOp",EDGE,"E67.5.0")])]})]});
            var Q27;
            Q27=makeQuery(id+"F10.boolean.opBoolean","INTERSECT",EDGE,{"disambiguationData":[OD(1.0)],"derivedFrom":[makeQuery(id+"F6.opRevolve","SWEPT_FACE",FACE,{"disambiguationData":[OSD([sQuery(id+"F4.wireOp",EDGE,"E51")])]}),makeQuery(id+"F10.opExtrude","SWEPT_FACE",FACE,{"disambiguationData":[OSD([sQuery(id+"F9.wireOp",EDGE,"E67.4.0")])]})]});
            var Q28;
            Q28=makeQuery(id+"F10.boolean.opBoolean","INTERSECT",EDGE,{"disambiguationData":[OD(1.0)],"derivedFrom":[makeQuery(id+"F6.opRevolve","SWEPT_FACE",FACE,{"disambiguationData":[OSD([sQuery(id+"F4.wireOp",EDGE,"E51")])]}),makeQuery(id+"F10.opExtrude","SWEPT_FACE",FACE,{"disambiguationData":[OSD([sQuery(id+"F9.wireOp",EDGE,"E67.3.0")])]})]});
            var Q29;
            Q29=makeQuery(id+"F10.boolean.opBoolean","INTERSECT",EDGE,{"disambiguationData":[OD(1.0)],"derivedFrom":[makeQuery(id+"F6.opRevolve","SWEPT_FACE",FACE,{"disambiguationData":[OSD([sQuery(id+"F4.wireOp",EDGE,"E51")])]}),makeQuery(id+"F10.opExtrude","SWEPT_FACE",FACE,{"disambiguationData":[OSD([sQuery(id+"F9.wireOp",EDGE,"E67.2.0")])]})]});
            var Q30;
            Q30=makeQuery(id+"F10.boolean.opBoolean","INTERSECT",EDGE,{"disambiguationData":[OD(1.0)],"derivedFrom":[makeQuery(id+"F6.opRevolve","SWEPT_FACE",FACE,{"disambiguationData":[OSD([sQuery(id+"F4.wireOp",EDGE,"E51")])]}),makeQuery(id+"F10.opExtrude","SWEPT_FACE",FACE,{"disambiguationData":[OSD([sQuery(id+"F9.wireOp",EDGE,"E67.1.0")])]})]});
            var Q31;
            Q31=makeQuery(id+"F10.boolean.opBoolean","INTERSECT",EDGE,{"disambiguationData":[OD(1.0)],"derivedFrom":[makeQuery(id+"F6.opRevolve","SWEPT_FACE",FACE,{"disambiguationData":[OSD([sQuery(id+"F4.wireOp",EDGE,"E51")])]}),makeQuery(id+"F10.opExtrude","SWEPT_FACE",FACE,{"disambiguationData":[OSD([sQuery(id+"F9.wireOp",EDGE,"E65")])]})]});
            var Q32;
            Q32=makeQuery(id+"F10.boolean.opBoolean","INTERSECT",EDGE,{"disambiguationData":[OD(0.0)],"derivedFrom":[makeQuery(id+"F6.opRevolve","SWEPT_FACE",FACE,{"disambiguationData":[OSD([sQuery(id+"F4.wireOp",EDGE,"E51")])]}),makeQuery(id+"F10.opExtrude","SWEPT_FACE",FACE,{"disambiguationData":[OSD([sQuery(id+"F9.wireOp",EDGE,"E65")])]})]});
            var Q33;
            Q33=makeQuery(id+"F10.boolean.opBoolean","INTERSECT",EDGE,{"disambiguationData":[OD(0.0)],"derivedFrom":[makeQuery(id+"F6.opRevolve","SWEPT_FACE",FACE,{"disambiguationData":[OSD([sQuery(id+"F4.wireOp",EDGE,"E51")])]}),makeQuery(id+"F10.opExtrude","SWEPT_FACE",FACE,{"disambiguationData":[OSD([sQuery(id+"F9.wireOp",EDGE,"E67.1.0")])]})]});
            var Q34;
            Q34=makeQuery(id+"F10.boolean.opBoolean","INTERSECT",EDGE,{"disambiguationData":[OD(0.0)],"derivedFrom":[makeQuery(id+"F6.opRevolve","SWEPT_FACE",FACE,{"disambiguationData":[OSD([sQuery(id+"F4.wireOp",EDGE,"E51")])]}),makeQuery(id+"F10.opExtrude","SWEPT_FACE",FACE,{"disambiguationData":[OSD([sQuery(id+"F9.wireOp",EDGE,"E67.2.0")])]})]});
            var Q35;
            Q35=makeQuery(id+"F10.boolean.opBoolean","INTERSECT",EDGE,{"disambiguationData":[OD(0.0)],"derivedFrom":[makeQuery(id+"F6.opRevolve","SWEPT_FACE",FACE,{"disambiguationData":[OSD([sQuery(id+"F4.wireOp",EDGE,"E51")])]}),makeQuery(id+"F10.opExtrude","SWEPT_FACE",FACE,{"disambiguationData":[OSD([sQuery(id+"F9.wireOp",EDGE,"E67.3.0")])]})]});
            var Q36;
            Q36=makeQuery(id+"F10.boolean.opBoolean","INTERSECT",EDGE,{"disambiguationData":[OD(0.0)],"derivedFrom":[makeQuery(id+"F6.opRevolve","SWEPT_FACE",FACE,{"disambiguationData":[OSD([sQuery(id+"F4.wireOp",EDGE,"E51")])]}),makeQuery(id+"F10.opExtrude","SWEPT_FACE",FACE,{"disambiguationData":[OSD([sQuery(id+"F9.wireOp",EDGE,"E67.4.0")])]})]});
            var Q37;
            Q37=makeQuery(id+"F10.boolean.opBoolean","INTERSECT",EDGE,{"disambiguationData":[OD(0.0)],"derivedFrom":[makeQuery(id+"F6.opRevolve","SWEPT_FACE",FACE,{"disambiguationData":[OSD([sQuery(id+"F4.wireOp",EDGE,"E51")])]}),makeQuery(id+"F10.opExtrude","SWEPT_FACE",FACE,{"disambiguationData":[OSD([sQuery(id+"F9.wireOp",EDGE,"E67.5.0")])]})]});
            var Q38;
            Q38=makeQuery(id+"F10.boolean.opBoolean","INTERSECT",EDGE,{"disambiguationData":[OD(0.0)],"derivedFrom":[makeQuery(id+"F6.opRevolve","SWEPT_FACE",FACE,{"disambiguationData":[OSD([sQuery(id+"F4.wireOp",EDGE,"E51")])]}),makeQuery(id+"F10.opExtrude","SWEPT_FACE",FACE,{"disambiguationData":[OSD([sQuery(id+"F9.wireOp",EDGE,"E67.6.0")])]})]});
            var Q39;
            Q39=makeQuery(id+"F10.boolean.opBoolean","INTERSECT",EDGE,{"disambiguationData":[OD(1.0)],"derivedFrom":[makeQuery(id+"F6.opRevolve","SWEPT_FACE",FACE,{"disambiguationData":[OSD([sQuery(id+"F4.wireOp",EDGE,"E51")])]}),makeQuery(id+"F10.opExtrude","SWEPT_FACE",FACE,{"disambiguationData":[OSD([sQuery(id+"F9.wireOp",EDGE,"E67.7.0")])]})]});
            var Q40;
            {var subQ0=sQuery(id+"F4.wireOp",EDGE,"E51");var subQ1=sQuery(id+"F4.wireOp",EDGE,"E53");Q40=makeQuery(id+"F10.boolean.opBoolean","SPLIT",EDGE,{"disambiguationData":[TD([makeQuery(id+"F1.opExtrude","SWEPT_FACE",FACE,{"disambiguationData":[OSD([sQuery(id+"F0.wireOp",EDGE,"E20")])]}),makeQuery(id+"F6.opRevolve","SWEPT_FACE",FACE,{"disambiguationData":[OSD([subQ0])]}),makeQuery(id+"F6.opRevolve","SWEPT_FACE",FACE,{"disambiguationData":[OSD([subQ1])]}),makeQuery(id+"F10.opExtrude","SWEPT_FACE",FACE,{"disambiguationData":[OSD([sQuery(id+"F9.wireOp",EDGE,"E67.7.0")])]})])],"derivedFrom":makeQuery(id+"F6.opRevolve","SWEPT_EDGE",EDGE,{"disambiguationData":[OSD([subQ0,subQ1])]})});}
            var Q41;
            {var subQ0=sQuery(id+"F4.wireOp",EDGE,"E51");var subQ1=sQuery(id+"F4.wireOp",EDGE,"E53");Q41=makeQuery(id+"F10.boolean.opBoolean","SPLIT",EDGE,{"disambiguationData":[TD([makeQuery(id+"F6.opRevolve","SWEPT_FACE",FACE,{"disambiguationData":[OSD([subQ0])]}),makeQuery(id+"F6.opRevolve","SWEPT_FACE",FACE,{"disambiguationData":[OSD([subQ1])]}),makeQuery(id+"F10.opExtrude","SWEPT_FACE",FACE,{"disambiguationData":[OSD([sQuery(id+"F9.wireOp",EDGE,"E67.6.0")])]}),makeQuery(id+"F10.opExtrude","SWEPT_FACE",FACE,{"disambiguationData":[OSD([sQuery(id+"F9.wireOp",EDGE,"E67.7.0")])]})])],"derivedFrom":makeQuery(id+"F6.opRevolve","SWEPT_EDGE",EDGE,{"disambiguationData":[OSD([subQ0,subQ1])]})});}
            var Q42;
            {var subQ0=sQuery(id+"F4.wireOp",EDGE,"E51");var subQ1=sQuery(id+"F4.wireOp",EDGE,"E53");Q42=makeQuery(id+"F10.boolean.opBoolean","SPLIT",EDGE,{"disambiguationData":[TD([makeQuery(id+"F6.opRevolve","SWEPT_FACE",FACE,{"disambiguationData":[OSD([subQ0])]}),makeQuery(id+"F6.opRevolve","SWEPT_FACE",FACE,{"disambiguationData":[OSD([subQ1])]}),makeQuery(id+"F10.opExtrude","SWEPT_FACE",FACE,{"disambiguationData":[OSD([sQuery(id+"F9.wireOp",EDGE,"E67.5.0")])]}),makeQuery(id+"F10.opExtrude","SWEPT_FACE",FACE,{"disambiguationData":[OSD([sQuery(id+"F9.wireOp",EDGE,"E67.6.0")])]})])],"derivedFrom":makeQuery(id+"F6.opRevolve","SWEPT_EDGE",EDGE,{"disambiguationData":[OSD([subQ0,subQ1])]})});}
            var Q43;
            {var subQ0=sQuery(id+"F4.wireOp",EDGE,"E51");var subQ1=sQuery(id+"F4.wireOp",EDGE,"E53");Q43=makeQuery(id+"F10.boolean.opBoolean","SPLIT",EDGE,{"disambiguationData":[TD([makeQuery(id+"F6.opRevolve","SWEPT_FACE",FACE,{"disambiguationData":[OSD([subQ0])]}),makeQuery(id+"F6.opRevolve","SWEPT_FACE",FACE,{"disambiguationData":[OSD([subQ1])]}),makeQuery(id+"F10.opExtrude","SWEPT_FACE",FACE,{"disambiguationData":[OSD([sQuery(id+"F9.wireOp",EDGE,"E67.4.0")])]}),makeQuery(id+"F10.opExtrude","SWEPT_FACE",FACE,{"disambiguationData":[OSD([sQuery(id+"F9.wireOp",EDGE,"E67.5.0")])]})])],"derivedFrom":makeQuery(id+"F6.opRevolve","SWEPT_EDGE",EDGE,{"disambiguationData":[OSD([subQ0,subQ1])]})});}
            var Q44;
            {var subQ0=sQuery(id+"F4.wireOp",EDGE,"E51");var subQ1=sQuery(id+"F4.wireOp",EDGE,"E53");Q44=makeQuery(id+"F10.boolean.opBoolean","SPLIT",EDGE,{"disambiguationData":[TD([makeQuery(id+"F6.opRevolve","SWEPT_FACE",FACE,{"disambiguationData":[OSD([subQ0])]}),makeQuery(id+"F6.opRevolve","SWEPT_FACE",FACE,{"disambiguationData":[OSD([subQ1])]}),makeQuery(id+"F10.opExtrude","SWEPT_FACE",FACE,{"disambiguationData":[OSD([sQuery(id+"F9.wireOp",EDGE,"E67.3.0")])]}),makeQuery(id+"F10.opExtrude","SWEPT_FACE",FACE,{"disambiguationData":[OSD([sQuery(id+"F9.wireOp",EDGE,"E67.4.0")])]})])],"derivedFrom":makeQuery(id+"F6.opRevolve","SWEPT_EDGE",EDGE,{"disambiguationData":[OSD([subQ0,subQ1])]})});}
            var Q45;
            {var subQ0=sQuery(id+"F4.wireOp",EDGE,"E51");var subQ1=sQuery(id+"F4.wireOp",EDGE,"E53");Q45=makeQuery(id+"F10.boolean.opBoolean","SPLIT",EDGE,{"disambiguationData":[TD([makeQuery(id+"F6.opRevolve","SWEPT_FACE",FACE,{"disambiguationData":[OSD([subQ0])]}),makeQuery(id+"F6.opRevolve","SWEPT_FACE",FACE,{"disambiguationData":[OSD([subQ1])]}),makeQuery(id+"F10.opExtrude","SWEPT_FACE",FACE,{"disambiguationData":[OSD([sQuery(id+"F9.wireOp",EDGE,"E67.2.0")])]}),makeQuery(id+"F10.opExtrude","SWEPT_FACE",FACE,{"disambiguationData":[OSD([sQuery(id+"F9.wireOp",EDGE,"E67.3.0")])]})])],"derivedFrom":makeQuery(id+"F6.opRevolve","SWEPT_EDGE",EDGE,{"disambiguationData":[OSD([subQ0,subQ1])]})});}
            var Q46;
            {var subQ0=sQuery(id+"F4.wireOp",EDGE,"E51");var subQ1=sQuery(id+"F4.wireOp",EDGE,"E53");Q46=makeQuery(id+"F10.boolean.opBoolean","SPLIT",EDGE,{"disambiguationData":[TD([makeQuery(id+"F6.opRevolve","SWEPT_FACE",FACE,{"disambiguationData":[OSD([subQ0])]}),makeQuery(id+"F6.opRevolve","SWEPT_FACE",FACE,{"disambiguationData":[OSD([subQ1])]}),makeQuery(id+"F10.opExtrude","SWEPT_FACE",FACE,{"disambiguationData":[OSD([sQuery(id+"F9.wireOp",EDGE,"E67.1.0")])]}),makeQuery(id+"F10.opExtrude","SWEPT_FACE",FACE,{"disambiguationData":[OSD([sQuery(id+"F9.wireOp",EDGE,"E67.2.0")])]})])],"derivedFrom":makeQuery(id+"F6.opRevolve","SWEPT_EDGE",EDGE,{"disambiguationData":[OSD([subQ0,subQ1])]})});}
            var Q47;
            {var subQ0=sQuery(id+"F4.wireOp",EDGE,"E51");var subQ1=sQuery(id+"F4.wireOp",EDGE,"E53");Q47=makeQuery(id+"F10.boolean.opBoolean","SPLIT",EDGE,{"disambiguationData":[TD([makeQuery(id+"F6.opRevolve","SWEPT_FACE",FACE,{"disambiguationData":[OSD([subQ0])]}),makeQuery(id+"F6.opRevolve","SWEPT_FACE",FACE,{"disambiguationData":[OSD([subQ1])]}),makeQuery(id+"F10.opExtrude","SWEPT_FACE",FACE,{"disambiguationData":[OSD([sQuery(id+"F9.wireOp",EDGE,"E65")])]}),makeQuery(id+"F10.opExtrude","SWEPT_FACE",FACE,{"disambiguationData":[OSD([sQuery(id+"F9.wireOp",EDGE,"E67.1.0")])]})])],"derivedFrom":makeQuery(id+"F6.opRevolve","SWEPT_EDGE",EDGE,{"disambiguationData":[OSD([subQ0,subQ1])]})});}
            var Q48;
            {var subQ0=sQuery(id+"F4.wireOp",EDGE,"E51");var subQ1=sQuery(id+"F4.wireOp",EDGE,"E53");Q48=makeQuery(id+"F10.boolean.opBoolean","SPLIT",EDGE,{"disambiguationData":[TD([makeQuery(id+"F1.opExtrude","SWEPT_FACE",FACE,{"disambiguationData":[OSD([sQuery(id+"F0.wireOp",EDGE,"E21"),sQuery(id+"F0.wireOp",EDGE,"E25"),sQuery(id+"F0.wireOp",EDGE,"E26")])]}),makeQuery(id+"F6.opRevolve","SWEPT_FACE",FACE,{"disambiguationData":[OSD([subQ0])]}),makeQuery(id+"F6.opRevolve","SWEPT_FACE",FACE,{"disambiguationData":[OSD([subQ1])]}),makeQuery(id+"F10.opExtrude","SWEPT_FACE",FACE,{"disambiguationData":[OSD([sQuery(id+"F9.wireOp",EDGE,"E65")])]})])],"derivedFrom":makeQuery(id+"F6.opRevolve","SWEPT_EDGE",EDGE,{"disambiguationData":[OSD([subQ0,subQ1])]})});}
            fillet(context, id + "F11", {"entities" : qUnion([Q0, Q1, Q2, Q3, Q4, Q5, Q6, Q7, Q8, Q9, Q10, Q11, Q12, Q13, Q14, Q15, Q16, Q17, Q18, Q19, Q20, Q21, Q22, Q23, Q24, Q25, Q26, Q27, Q28, Q29, Q30, Q31, Q32, Q33, Q34, Q35, Q36, Q37, Q38, Q39, Q40, Q41, Q42, Q43, Q44, Q45, Q46, Q47, Q48]), "radius" : 1 * mm, "tangentPropagation" : true, "allowEdgeOverflow" : false});
        }
        {
            var Q0;
            {var subQ0=sQuery(id+"F4.wireOp",EDGE,"E51");var subQ1=makeQuery(id+"F6.opRevolve","SWEPT_FACE",FACE,{"disambiguationData":[OSD([subQ0])]});var subQ2=sQuery(id+"F4.wireOp",EDGE,"E53");var subQ3=makeQuery(id+"F10.opExtrude","SWEPT_FACE",FACE,{"disambiguationData":[OSD([sQuery(id+"F9.wireOp",EDGE,"E67.5.0")])]});Q0=makeQuery(id+"F11.opFillet","BLEND_EDGE",EDGE,{"blendedFrom":[makeQuery(id+"F10.boolean.opBoolean","INTERSECT",EDGE,{"disambiguationData":[OD(0.0)],"derivedFrom":[subQ1,subQ3]}),makeQuery(id+"F10.boolean.opBoolean","SPLIT",EDGE,{"disambiguationData":[TD([subQ1,makeQuery(id+"F6.opRevolve","SWEPT_FACE",FACE,{"disambiguationData":[OSD([subQ2])]}),makeQuery(id+"F10.opExtrude","SWEPT_FACE",FACE,{"disambiguationData":[OSD([sQuery(id+"F9.wireOp",EDGE,"E67.4.0")])]}),subQ3])],"derivedFrom":makeQuery(id+"F6.opRevolve","SWEPT_EDGE",EDGE,{"disambiguationData":[OSD([subQ0,subQ2])]})})],"blendedInto":[]});}
            var Q1;
            {var subQ0=sQuery(id+"F4.wireOp",EDGE,"E51");var subQ1=makeQuery(id+"F6.opRevolve","SWEPT_FACE",FACE,{"disambiguationData":[OSD([subQ0])]});var subQ2=sQuery(id+"F4.wireOp",EDGE,"E53");Q1=makeQuery(id+"F11.opFillet","BLEND_EDGE",EDGE,{"blendedFrom":[makeQuery(id+"F8.boolean.opBoolean","INTERSECT",EDGE,{"derivedFrom":[subQ1,makeQuery(id+"F8.opExtrude","SWEPT_FACE",FACE,{"disambiguationData":[OSD([sQuery(id+"F7.wireOp",EDGE,"E57.3")])]})]}),makeQuery(id+"F10.boolean.opBoolean","SPLIT",EDGE,{"disambiguationData":[TD([makeQuery(id+"F1.opExtrude","SWEPT_FACE",FACE,{"disambiguationData":[OSD([sQuery(id+"F0.wireOp",EDGE,"E20")])]}),subQ1,makeQuery(id+"F6.opRevolve","SWEPT_FACE",FACE,{"disambiguationData":[OSD([subQ2])]}),makeQuery(id+"F10.opExtrude","SWEPT_FACE",FACE,{"disambiguationData":[OSD([sQuery(id+"F9.wireOp",EDGE,"E67.7.0")])]})])],"derivedFrom":makeQuery(id+"F6.opRevolve","SWEPT_EDGE",EDGE,{"disambiguationData":[OSD([subQ0,subQ2])]})})],"blendedInto":[]});}
            var Q2;
            {var subQ0=makeQuery(id+"F10.opExtrude","SWEPT_FACE",FACE,{"disambiguationData":[OSD([sQuery(id+"F9.wireOp",EDGE,"E67.7.0")])]});var subQ1=sQuery(id+"F4.wireOp",EDGE,"E51");var subQ2=makeQuery(id+"F6.opRevolve","SWEPT_FACE",FACE,{"disambiguationData":[OSD([subQ1])]});var subQ3=sQuery(id+"F4.wireOp",EDGE,"E53");Q2=makeQuery(id+"F11.opFillet","BLEND_EDGE",EDGE,{"blendedFrom":[makeQuery(id+"F10.boolean.opBoolean","SPLIT",EDGE,{"disambiguationData":[TD([makeQuery(id+"F1.opExtrude","SWEPT_FACE",FACE,{"disambiguationData":[OSD([sQuery(id+"F0.wireOp",EDGE,"E20")])]}),subQ2,makeQuery(id+"F6.opRevolve","SWEPT_FACE",FACE,{"disambiguationData":[OSD([subQ3])]}),subQ0])],"derivedFrom":makeQuery(id+"F6.opRevolve","SWEPT_EDGE",EDGE,{"disambiguationData":[OSD([subQ1,subQ3])]})}),makeQuery(id+"F10.boolean.opBoolean","INTERSECT",EDGE,{"disambiguationData":[OD(0.0)],"derivedFrom":[subQ2,subQ0]})],"blendedInto":[]});}
            var Q3;
            {var subQ0=sQuery(id+"F4.wireOp",EDGE,"E51");var subQ1=makeQuery(id+"F6.opRevolve","SWEPT_FACE",FACE,{"disambiguationData":[OSD([subQ0])]});var subQ2=sQuery(id+"F4.wireOp",EDGE,"E53");var subQ3=makeQuery(id+"F10.opExtrude","SWEPT_FACE",FACE,{"disambiguationData":[OSD([sQuery(id+"F9.wireOp",EDGE,"E67.7.0")])]});Q3=makeQuery(id+"F11.opFillet","BLEND_EDGE",EDGE,{"blendedFrom":[makeQuery(id+"F10.boolean.opBoolean","INTERSECT",EDGE,{"disambiguationData":[OD(1.0)],"derivedFrom":[subQ1,subQ3]}),makeQuery(id+"F10.boolean.opBoolean","SPLIT",EDGE,{"disambiguationData":[TD([subQ1,makeQuery(id+"F6.opRevolve","SWEPT_FACE",FACE,{"disambiguationData":[OSD([subQ2])]}),makeQuery(id+"F10.opExtrude","SWEPT_FACE",FACE,{"disambiguationData":[OSD([sQuery(id+"F9.wireOp",EDGE,"E67.6.0")])]}),subQ3])],"derivedFrom":makeQuery(id+"F6.opRevolve","SWEPT_EDGE",EDGE,{"disambiguationData":[OSD([subQ0,subQ2])]})})],"blendedInto":[]});}
            var Q4;
            {var subQ0=sQuery(id+"F4.wireOp",EDGE,"E51");var subQ1=makeQuery(id+"F6.opRevolve","SWEPT_FACE",FACE,{"disambiguationData":[OSD([subQ0])]});var subQ2=sQuery(id+"F4.wireOp",EDGE,"E53");var subQ3=makeQuery(id+"F10.opExtrude","SWEPT_FACE",FACE,{"disambiguationData":[OSD([sQuery(id+"F9.wireOp",EDGE,"E67.6.0")])]});Q4=makeQuery(id+"F11.opFillet","BLEND_EDGE",EDGE,{"blendedFrom":[makeQuery(id+"F10.boolean.opBoolean","INTERSECT",EDGE,{"disambiguationData":[OD(1.0)],"derivedFrom":[subQ1,subQ3]}),makeQuery(id+"F10.boolean.opBoolean","SPLIT",EDGE,{"disambiguationData":[TD([subQ1,makeQuery(id+"F6.opRevolve","SWEPT_FACE",FACE,{"disambiguationData":[OSD([subQ2])]}),subQ3,makeQuery(id+"F10.opExtrude","SWEPT_FACE",FACE,{"disambiguationData":[OSD([sQuery(id+"F9.wireOp",EDGE,"E67.7.0")])]})])],"derivedFrom":makeQuery(id+"F6.opRevolve","SWEPT_EDGE",EDGE,{"disambiguationData":[OSD([subQ0,subQ2])]})})],"blendedInto":[]});}
            var Q5;
            {var subQ0=sQuery(id+"F4.wireOp",EDGE,"E51");var subQ1=makeQuery(id+"F6.opRevolve","SWEPT_FACE",FACE,{"disambiguationData":[OSD([subQ0])]});var subQ2=sQuery(id+"F4.wireOp",EDGE,"E53");var subQ3=makeQuery(id+"F10.opExtrude","SWEPT_FACE",FACE,{"disambiguationData":[OSD([sQuery(id+"F9.wireOp",EDGE,"E67.6.0")])]});Q5=makeQuery(id+"F11.opFillet","BLEND_EDGE",EDGE,{"blendedFrom":[makeQuery(id+"F10.boolean.opBoolean","INTERSECT",EDGE,{"disambiguationData":[OD(0.0)],"derivedFrom":[subQ1,subQ3]}),makeQuery(id+"F10.boolean.opBoolean","SPLIT",EDGE,{"disambiguationData":[TD([subQ1,makeQuery(id+"F6.opRevolve","SWEPT_FACE",FACE,{"disambiguationData":[OSD([subQ2])]}),makeQuery(id+"F10.opExtrude","SWEPT_FACE",FACE,{"disambiguationData":[OSD([sQuery(id+"F9.wireOp",EDGE,"E67.5.0")])]}),subQ3])],"derivedFrom":makeQuery(id+"F6.opRevolve","SWEPT_EDGE",EDGE,{"disambiguationData":[OSD([subQ0,subQ2])]})})],"blendedInto":[]});}
            var Q6;
            {var subQ0=sQuery(id+"F4.wireOp",EDGE,"E51");var subQ1=makeQuery(id+"F6.opRevolve","SWEPT_FACE",FACE,{"disambiguationData":[OSD([subQ0])]});var subQ2=sQuery(id+"F4.wireOp",EDGE,"E53");var subQ3=makeQuery(id+"F10.opExtrude","SWEPT_FACE",FACE,{"disambiguationData":[OSD([sQuery(id+"F9.wireOp",EDGE,"E67.5.0")])]});Q6=makeQuery(id+"F11.opFillet","BLEND_EDGE",EDGE,{"blendedFrom":[makeQuery(id+"F10.boolean.opBoolean","INTERSECT",EDGE,{"disambiguationData":[OD(1.0)],"derivedFrom":[subQ1,subQ3]}),makeQuery(id+"F10.boolean.opBoolean","SPLIT",EDGE,{"disambiguationData":[TD([subQ1,makeQuery(id+"F6.opRevolve","SWEPT_FACE",FACE,{"disambiguationData":[OSD([subQ2])]}),subQ3,makeQuery(id+"F10.opExtrude","SWEPT_FACE",FACE,{"disambiguationData":[OSD([sQuery(id+"F9.wireOp",EDGE,"E67.6.0")])]})])],"derivedFrom":makeQuery(id+"F6.opRevolve","SWEPT_EDGE",EDGE,{"disambiguationData":[OSD([subQ0,subQ2])]})})],"blendedInto":[]});}
            var Q7;
            {var subQ0=sQuery(id+"F4.wireOp",EDGE,"E51");var subQ1=makeQuery(id+"F6.opRevolve","SWEPT_FACE",FACE,{"disambiguationData":[OSD([subQ0])]});var subQ2=makeQuery(id+"F10.opExtrude","SWEPT_FACE",FACE,{"disambiguationData":[OSD([sQuery(id+"F9.wireOp",EDGE,"E67.4.0")])]});var subQ3=sQuery(id+"F4.wireOp",EDGE,"E53");Q7=makeQuery(id+"F11.opFillet","BLEND_EDGE",EDGE,{"blendedFrom":[makeQuery(id+"F10.boolean.opBoolean","INTERSECT",EDGE,{"disambiguationData":[OD(1.0)],"derivedFrom":[subQ1,subQ2]}),makeQuery(id+"F10.boolean.opBoolean","SPLIT",EDGE,{"disambiguationData":[TD([subQ1,makeQuery(id+"F6.opRevolve","SWEPT_FACE",FACE,{"disambiguationData":[OSD([subQ3])]}),subQ2,makeQuery(id+"F10.opExtrude","SWEPT_FACE",FACE,{"disambiguationData":[OSD([sQuery(id+"F9.wireOp",EDGE,"E67.5.0")])]})])],"derivedFrom":makeQuery(id+"F6.opRevolve","SWEPT_EDGE",EDGE,{"disambiguationData":[OSD([subQ0,subQ3])]})})],"blendedInto":[]});}
            var Q8;
            {var subQ0=sQuery(id+"F4.wireOp",EDGE,"E51");var subQ1=makeQuery(id+"F6.opRevolve","SWEPT_FACE",FACE,{"disambiguationData":[OSD([subQ0])]});var subQ2=makeQuery(id+"F10.opExtrude","SWEPT_FACE",FACE,{"disambiguationData":[OSD([sQuery(id+"F9.wireOp",EDGE,"E67.4.0")])]});var subQ3=sQuery(id+"F4.wireOp",EDGE,"E53");Q8=makeQuery(id+"F11.opFillet","BLEND_EDGE",EDGE,{"blendedFrom":[makeQuery(id+"F10.boolean.opBoolean","INTERSECT",EDGE,{"disambiguationData":[OD(0.0)],"derivedFrom":[subQ1,subQ2]}),makeQuery(id+"F10.boolean.opBoolean","SPLIT",EDGE,{"disambiguationData":[TD([subQ1,makeQuery(id+"F6.opRevolve","SWEPT_FACE",FACE,{"disambiguationData":[OSD([subQ3])]}),makeQuery(id+"F10.opExtrude","SWEPT_FACE",FACE,{"disambiguationData":[OSD([sQuery(id+"F9.wireOp",EDGE,"E67.3.0")])]}),subQ2])],"derivedFrom":makeQuery(id+"F6.opRevolve","SWEPT_EDGE",EDGE,{"disambiguationData":[OSD([subQ0,subQ3])]})})],"blendedInto":[]});}
            var Q9;
            {var subQ0=sQuery(id+"F4.wireOp",EDGE,"E51");var subQ1=makeQuery(id+"F6.opRevolve","SWEPT_FACE",FACE,{"disambiguationData":[OSD([subQ0])]});var subQ2=sQuery(id+"F4.wireOp",EDGE,"E53");var subQ3=makeQuery(id+"F10.opExtrude","SWEPT_FACE",FACE,{"disambiguationData":[OSD([sQuery(id+"F9.wireOp",EDGE,"E67.3.0")])]});Q9=makeQuery(id+"F11.opFillet","BLEND_EDGE",EDGE,{"blendedFrom":[makeQuery(id+"F10.boolean.opBoolean","INTERSECT",EDGE,{"disambiguationData":[OD(1.0)],"derivedFrom":[subQ1,subQ3]}),makeQuery(id+"F10.boolean.opBoolean","SPLIT",EDGE,{"disambiguationData":[TD([subQ1,makeQuery(id+"F6.opRevolve","SWEPT_FACE",FACE,{"disambiguationData":[OSD([subQ2])]}),subQ3,makeQuery(id+"F10.opExtrude","SWEPT_FACE",FACE,{"disambiguationData":[OSD([sQuery(id+"F9.wireOp",EDGE,"E67.4.0")])]})])],"derivedFrom":makeQuery(id+"F6.opRevolve","SWEPT_EDGE",EDGE,{"disambiguationData":[OSD([subQ0,subQ2])]})})],"blendedInto":[]});}
            var Q10;
            {var subQ0=sQuery(id+"F4.wireOp",EDGE,"E51");var subQ1=makeQuery(id+"F6.opRevolve","SWEPT_FACE",FACE,{"disambiguationData":[OSD([subQ0])]});var subQ2=sQuery(id+"F4.wireOp",EDGE,"E53");var subQ3=makeQuery(id+"F10.opExtrude","SWEPT_FACE",FACE,{"disambiguationData":[OSD([sQuery(id+"F9.wireOp",EDGE,"E67.3.0")])]});Q10=makeQuery(id+"F11.opFillet","BLEND_EDGE",EDGE,{"blendedFrom":[makeQuery(id+"F10.boolean.opBoolean","INTERSECT",EDGE,{"disambiguationData":[OD(0.0)],"derivedFrom":[subQ1,subQ3]}),makeQuery(id+"F10.boolean.opBoolean","SPLIT",EDGE,{"disambiguationData":[TD([subQ1,makeQuery(id+"F6.opRevolve","SWEPT_FACE",FACE,{"disambiguationData":[OSD([subQ2])]}),makeQuery(id+"F10.opExtrude","SWEPT_FACE",FACE,{"disambiguationData":[OSD([sQuery(id+"F9.wireOp",EDGE,"E67.2.0")])]}),subQ3])],"derivedFrom":makeQuery(id+"F6.opRevolve","SWEPT_EDGE",EDGE,{"disambiguationData":[OSD([subQ0,subQ2])]})})],"blendedInto":[]});}
            var Q11;
            {var subQ0=sQuery(id+"F4.wireOp",EDGE,"E51");var subQ1=makeQuery(id+"F6.opRevolve","SWEPT_FACE",FACE,{"disambiguationData":[OSD([subQ0])]});var subQ2=sQuery(id+"F4.wireOp",EDGE,"E53");var subQ3=makeQuery(id+"F10.opExtrude","SWEPT_FACE",FACE,{"disambiguationData":[OSD([sQuery(id+"F9.wireOp",EDGE,"E67.2.0")])]});Q11=makeQuery(id+"F11.opFillet","BLEND_EDGE",EDGE,{"blendedFrom":[makeQuery(id+"F10.boolean.opBoolean","INTERSECT",EDGE,{"disambiguationData":[OD(1.0)],"derivedFrom":[subQ1,subQ3]}),makeQuery(id+"F10.boolean.opBoolean","SPLIT",EDGE,{"disambiguationData":[TD([subQ1,makeQuery(id+"F6.opRevolve","SWEPT_FACE",FACE,{"disambiguationData":[OSD([subQ2])]}),subQ3,makeQuery(id+"F10.opExtrude","SWEPT_FACE",FACE,{"disambiguationData":[OSD([sQuery(id+"F9.wireOp",EDGE,"E67.3.0")])]})])],"derivedFrom":makeQuery(id+"F6.opRevolve","SWEPT_EDGE",EDGE,{"disambiguationData":[OSD([subQ0,subQ2])]})})],"blendedInto":[]});}
            var Q12;
            {var subQ0=sQuery(id+"F4.wireOp",EDGE,"E51");var subQ1=makeQuery(id+"F6.opRevolve","SWEPT_FACE",FACE,{"disambiguationData":[OSD([subQ0])]});var subQ2=sQuery(id+"F4.wireOp",EDGE,"E53");var subQ3=makeQuery(id+"F10.opExtrude","SWEPT_FACE",FACE,{"disambiguationData":[OSD([sQuery(id+"F9.wireOp",EDGE,"E67.2.0")])]});Q12=makeQuery(id+"F11.opFillet","BLEND_EDGE",EDGE,{"blendedFrom":[makeQuery(id+"F10.boolean.opBoolean","INTERSECT",EDGE,{"disambiguationData":[OD(0.0)],"derivedFrom":[subQ1,subQ3]}),makeQuery(id+"F10.boolean.opBoolean","SPLIT",EDGE,{"disambiguationData":[TD([subQ1,makeQuery(id+"F6.opRevolve","SWEPT_FACE",FACE,{"disambiguationData":[OSD([subQ2])]}),makeQuery(id+"F10.opExtrude","SWEPT_FACE",FACE,{"disambiguationData":[OSD([sQuery(id+"F9.wireOp",EDGE,"E67.1.0")])]}),subQ3])],"derivedFrom":makeQuery(id+"F6.opRevolve","SWEPT_EDGE",EDGE,{"disambiguationData":[OSD([subQ0,subQ2])]})})],"blendedInto":[]});}
            var Q13;
            {var subQ0=sQuery(id+"F4.wireOp",EDGE,"E51");var subQ1=makeQuery(id+"F6.opRevolve","SWEPT_FACE",FACE,{"disambiguationData":[OSD([subQ0])]});var subQ2=sQuery(id+"F4.wireOp",EDGE,"E53");var subQ3=makeQuery(id+"F10.opExtrude","SWEPT_FACE",FACE,{"disambiguationData":[OSD([sQuery(id+"F9.wireOp",EDGE,"E67.1.0")])]});Q13=makeQuery(id+"F11.opFillet","BLEND_EDGE",EDGE,{"blendedFrom":[makeQuery(id+"F10.boolean.opBoolean","INTERSECT",EDGE,{"disambiguationData":[OD(1.0)],"derivedFrom":[subQ1,subQ3]}),makeQuery(id+"F10.boolean.opBoolean","SPLIT",EDGE,{"disambiguationData":[TD([subQ1,makeQuery(id+"F6.opRevolve","SWEPT_FACE",FACE,{"disambiguationData":[OSD([subQ2])]}),subQ3,makeQuery(id+"F10.opExtrude","SWEPT_FACE",FACE,{"disambiguationData":[OSD([sQuery(id+"F9.wireOp",EDGE,"E67.2.0")])]})])],"derivedFrom":makeQuery(id+"F6.opRevolve","SWEPT_EDGE",EDGE,{"disambiguationData":[OSD([subQ0,subQ2])]})})],"blendedInto":[]});}
            var Q14;
            {var subQ0=sQuery(id+"F4.wireOp",EDGE,"E51");var subQ1=makeQuery(id+"F6.opRevolve","SWEPT_FACE",FACE,{"disambiguationData":[OSD([subQ0])]});var subQ2=sQuery(id+"F4.wireOp",EDGE,"E53");var subQ3=makeQuery(id+"F10.opExtrude","SWEPT_FACE",FACE,{"disambiguationData":[OSD([sQuery(id+"F9.wireOp",EDGE,"E67.1.0")])]});Q14=makeQuery(id+"F11.opFillet","BLEND_EDGE",EDGE,{"blendedFrom":[makeQuery(id+"F10.boolean.opBoolean","INTERSECT",EDGE,{"disambiguationData":[OD(0.0)],"derivedFrom":[subQ1,subQ3]}),makeQuery(id+"F10.boolean.opBoolean","SPLIT",EDGE,{"disambiguationData":[TD([subQ1,makeQuery(id+"F6.opRevolve","SWEPT_FACE",FACE,{"disambiguationData":[OSD([subQ2])]}),makeQuery(id+"F10.opExtrude","SWEPT_FACE",FACE,{"disambiguationData":[OSD([sQuery(id+"F9.wireOp",EDGE,"E65")])]}),subQ3])],"derivedFrom":makeQuery(id+"F6.opRevolve","SWEPT_EDGE",EDGE,{"disambiguationData":[OSD([subQ0,subQ2])]})})],"blendedInto":[]});}
            var Q15;
            {var subQ0=sQuery(id+"F4.wireOp",EDGE,"E51");var subQ1=makeQuery(id+"F6.opRevolve","SWEPT_FACE",FACE,{"disambiguationData":[OSD([subQ0])]});var subQ2=sQuery(id+"F4.wireOp",EDGE,"E53");var subQ3=makeQuery(id+"F10.opExtrude","SWEPT_FACE",FACE,{"disambiguationData":[OSD([sQuery(id+"F9.wireOp",EDGE,"E65")])]});Q15=makeQuery(id+"F11.opFillet","BLEND_EDGE",EDGE,{"blendedFrom":[makeQuery(id+"F10.boolean.opBoolean","INTERSECT",EDGE,{"disambiguationData":[OD(1.0)],"derivedFrom":[subQ1,subQ3]}),makeQuery(id+"F10.boolean.opBoolean","SPLIT",EDGE,{"disambiguationData":[TD([subQ1,makeQuery(id+"F6.opRevolve","SWEPT_FACE",FACE,{"disambiguationData":[OSD([subQ2])]}),subQ3,makeQuery(id+"F10.opExtrude","SWEPT_FACE",FACE,{"disambiguationData":[OSD([sQuery(id+"F9.wireOp",EDGE,"E67.1.0")])]})])],"derivedFrom":makeQuery(id+"F6.opRevolve","SWEPT_EDGE",EDGE,{"disambiguationData":[OSD([subQ0,subQ2])]})})],"blendedInto":[]});}
            var Q16;
            {var subQ0=makeQuery(id+"F10.opExtrude","SWEPT_FACE",FACE,{"disambiguationData":[OSD([sQuery(id+"F9.wireOp",EDGE,"E65")])]});var subQ1=sQuery(id+"F4.wireOp",EDGE,"E51");var subQ2=makeQuery(id+"F6.opRevolve","SWEPT_FACE",FACE,{"disambiguationData":[OSD([subQ1])]});var subQ3=sQuery(id+"F4.wireOp",EDGE,"E53");Q16=makeQuery(id+"F11.opFillet","BLEND_EDGE",EDGE,{"blendedFrom":[makeQuery(id+"F10.boolean.opBoolean","SPLIT",EDGE,{"disambiguationData":[TD([makeQuery(id+"F1.opExtrude","SWEPT_FACE",FACE,{"disambiguationData":[OSD([sQuery(id+"F0.wireOp",EDGE,"E21"),sQuery(id+"F0.wireOp",EDGE,"E25"),sQuery(id+"F0.wireOp",EDGE,"E26")])]}),subQ2,makeQuery(id+"F6.opRevolve","SWEPT_FACE",FACE,{"disambiguationData":[OSD([subQ3])]}),subQ0])],"derivedFrom":makeQuery(id+"F6.opRevolve","SWEPT_EDGE",EDGE,{"disambiguationData":[OSD([subQ1,subQ3])]})}),makeQuery(id+"F10.boolean.opBoolean","INTERSECT",EDGE,{"disambiguationData":[OD(0.0)],"derivedFrom":[subQ2,subQ0]})],"blendedInto":[]});}
            var Q17;
            {var subQ0=sQuery(id+"F4.wireOp",EDGE,"E51");var subQ1=makeQuery(id+"F6.opRevolve","SWEPT_FACE",FACE,{"disambiguationData":[OSD([subQ0])]});var subQ2=sQuery(id+"F4.wireOp",EDGE,"E53");Q17=makeQuery(id+"F11.opFillet","BLEND_EDGE",EDGE,{"blendedFrom":[makeQuery(id+"F8.boolean.opBoolean","INTERSECT",EDGE,{"derivedFrom":[subQ1,makeQuery(id+"F8.opExtrude","SWEPT_FACE",FACE,{"disambiguationData":[OSD([sQuery(id+"F7.wireOp",EDGE,"E57.2")])]})]}),makeQuery(id+"F10.boolean.opBoolean","SPLIT",EDGE,{"disambiguationData":[TD([makeQuery(id+"F1.opExtrude","SWEPT_FACE",FACE,{"disambiguationData":[OSD([sQuery(id+"F0.wireOp",EDGE,"E21"),sQuery(id+"F0.wireOp",EDGE,"E25"),sQuery(id+"F0.wireOp",EDGE,"E26")])]}),subQ1,makeQuery(id+"F6.opRevolve","SWEPT_FACE",FACE,{"disambiguationData":[OSD([subQ2])]}),makeQuery(id+"F10.opExtrude","SWEPT_FACE",FACE,{"disambiguationData":[OSD([sQuery(id+"F9.wireOp",EDGE,"E65")])]})])],"derivedFrom":makeQuery(id+"F6.opRevolve","SWEPT_EDGE",EDGE,{"disambiguationData":[OSD([subQ0,subQ2])]})})],"blendedInto":[]});}
            fillet(context, id + "F12", {"entities" : qUnion([Q0, Q1, Q2, Q3, Q4, Q5, Q6, Q7, Q8, Q9, Q10, Q11, Q12, Q13, Q14, Q15, Q16, Q17]), "radius" : 1 * mm, "tangentPropagation" : true, "allowEdgeOverflow" : false});
        }
    });
